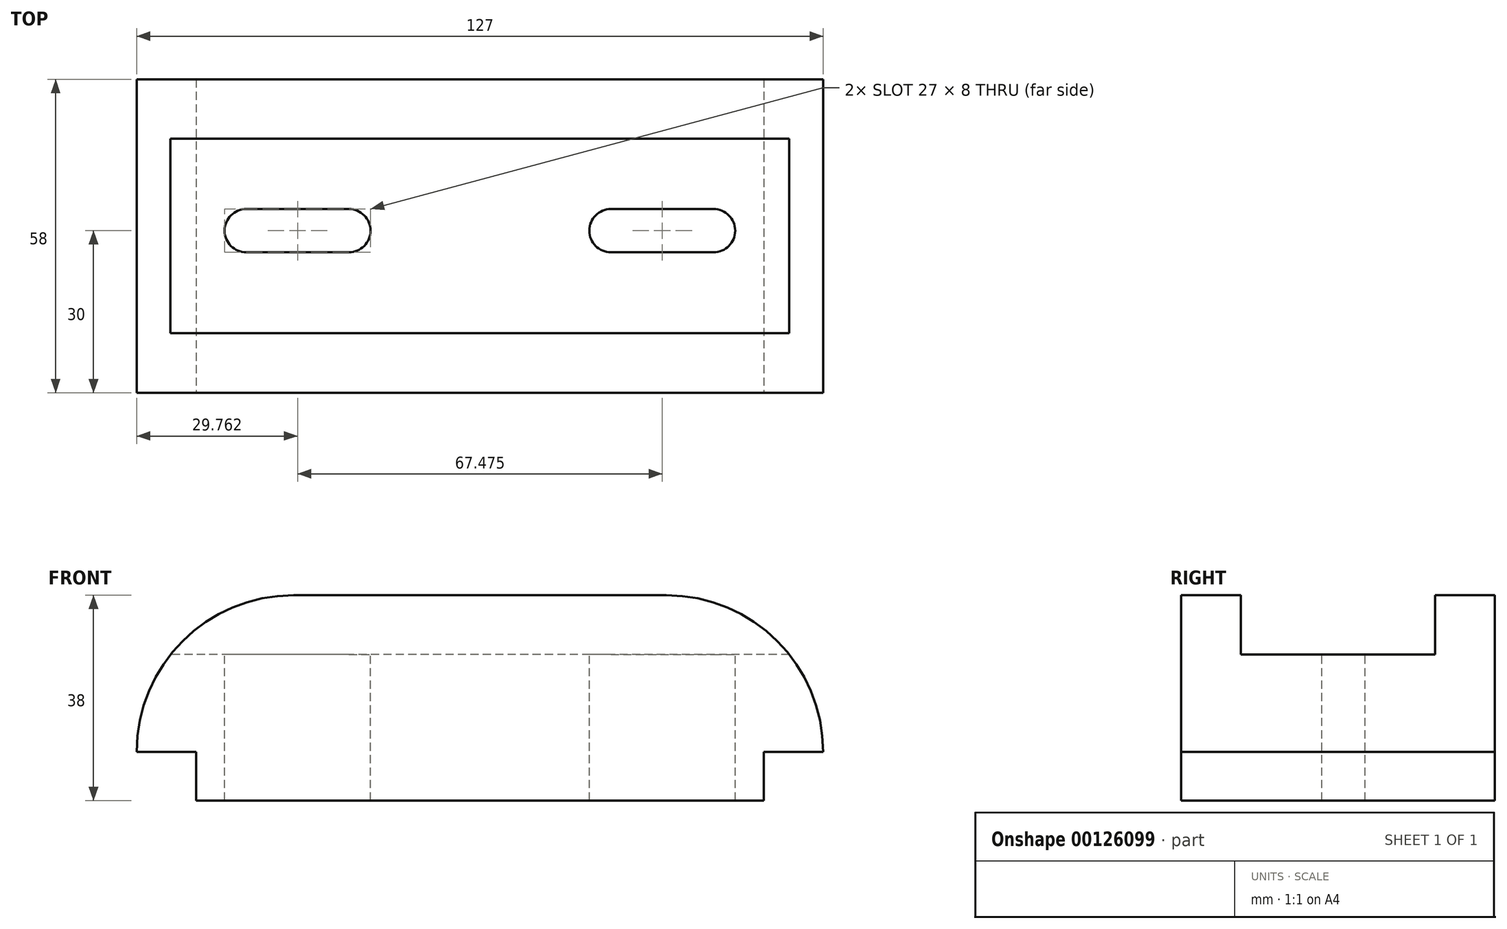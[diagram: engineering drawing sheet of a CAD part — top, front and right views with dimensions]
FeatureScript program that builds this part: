
annotation { "Feature Type Name" : "Feature", "Feature Type Description" : "" }
export const myFeature = defineFeature(function(context is Context, id is Id, definition is map)
    precondition{}
    {
        {
            var Q0;
            Q0=qCreatedBy(makeId("Front.planeOp"),FACE);
            var sketch = newSketch(context, id + "F0", { "sketchPlane" : qUnion([Q0])});
            skLineSegment(sketch, "E0", {"start": v(0, 72.55) * mm, "end": v(0, -38.1) * mm, "construction": true});
            skLineSegment(sketch, "E1", {"start": v(0, 38) * mm, "end": v(0, 0) * mm});
            skLineSegment(sketch, "E2", {"start": v(0, 0) * mm, "end": v(52.5, 0) * mm});
            skLineSegment(sketch, "E3", {"start": v(52.5, 0) * mm, "end": v(52.5, 9) * mm});
            skLineSegment(sketch, "E4", {"start": v(52.5, 9) * mm, "end": v(63.5, 9) * mm});
            skLineSegment(sketch, "E5", {"start": v(0, 38) * mm, "end": v(34.5, 38) * mm});
            skArc(sketch, "E6", {"start": v(34.5, 38) * mm, "mid": v(55, 29.5) * mm, "end": v(63.5, 9) * mm});
            skLineSegment(sketch, "E7.MirrorCS", {"start": v(0, 0) * mm, "end": v(-52.5, 0) * mm});
            skLineSegment(sketch, "E8.MirrorCS", {"start": v(-52.5, 0) * mm, "end": v(-52.5, 9) * mm});
            skLineSegment(sketch, "E9.MirrorCS", {"start": v(-52.5, 9) * mm, "end": v(-63.5, 9) * mm});
            skArc(sketch, "E10.MirrorCS", {"start": v(-34.5, 38) * mm, "mid": v(-55, 29.5) * mm, "end": v(-63.5, 9) * mm});
            skLineSegment(sketch, "E11.MirrorCS", {"start": v(0, 38) * mm, "end": v(-34.5, 38) * mm});
            skSolve(sketch);
        }
        {
            var Q0;
            Q0 = qSketchRegion(id + "F0", true);
            extrude(context, id + "F1", {"entities" : qUnion([Q0]), "oppositeDirection" : true, "depth" : 58 * mm});
        }
        {
            var Q0;
            Q0=makeQuery(id+"F1.opExtrude","SWEPT_FACE",FACE,{"disambiguationData":[OSD([sQuery(id+"F0.wireOp",EDGE,"E5"),sQuery(id+"F0.wireOp",EDGE,"E11.MirrorCS")])]});
            var sketch = newSketch(context, id + "F2", { "sketchPlane" : qUnion([Q0])});
            skLineSegment(sketch, "E12", {"start": v(0, 69.8) * mm, "end": v(0, -12.57) * mm, "construction": true});
            skPoint(sketch, "E12.startSnap0", {"position": v(0, 58) * mm});
            skPoint(sketch, "E12.endSnap0", {"position": v(0, 0) * mm});
            skLineSegment(sketch, "E13", {"start": v(63.5, 47) * mm, "end": v(63.5, 11) * mm});
            skLineSegment(sketch, "E14", {"start": v(63.5, 11) * mm, "end": v(0, 11) * mm});
            skLineSegment(sketch, "E15", {"start": v(0, 11) * mm, "end": v(0, 47) * mm});
            skLineSegment(sketch, "E16", {"start": v(0, 47) * mm, "end": v(63.5, 47) * mm});
            skLineSegment(sketch, "E17.MirrorCS", {"start": v(-63.5, 47) * mm, "end": v(-63.5, 11) * mm});
            skLineSegment(sketch, "E18.MirrorCS", {"start": v(-63.5, 11) * mm, "end": v(0, 11) * mm});
            skLineSegment(sketch, "E19.MirrorCS", {"start": v(0, 47) * mm, "end": v(-63.5, 47) * mm});
            skSolve(sketch);
        }
        {
            var Q0;
            Q0 = qSketchRegion(id + "F2", true);
            extrude(context, id + "F3", {"entities" : qUnion([Q0]), "operationType" : NewBodyOperationType.REMOVE, "oppositeDirection" : true, "depth" : 11 * mm});
        }
        {
            var Q0;
            Q0=makeQuery(id+"F3.boolean.opBoolean","COPY",FACE,{"derivedFrom":makeQuery(id+"F3.opExtrude","CAP_FACE",FACE,{"disambiguationData":[OSD([sQuery(id+"F2.wireOp",EDGE,"E13"),sQuery(id+"F2.wireOp",EDGE,"E14"),sQuery(id+"F2.wireOp",EDGE,"E16"),sQuery(id+"F2.wireOp",EDGE,"E17.MirrorCS"),sQuery(id+"F2.wireOp",EDGE,"E18.MirrorCS"),sQuery(id+"F2.wireOp",EDGE,"E19.MirrorCS")])],"isStart":false})});
            var sketch = newSketch(context, id + "F4", { "sketchPlane" : qUnion([Q0])});
            skLineSegment(sketch, "E20", {"start": v(24.24, 34) * mm, "end": v(43.24, 34) * mm});
            skLineSegment(sketch, "E21", {"start": v(24.24, 26) * mm, "end": v(43.24, 26) * mm});
            skArc(sketch, "E22", {"start": v(24.24, 34) * mm, "mid": v(20.24, 30) * mm, "end": v(24.24, 26) * mm});
            skArc(sketch, "E23", {"start": v(43.24, 34) * mm, "mid": v(47.24, 30) * mm, "end": v(43.24, 26) * mm});
            skLineSegment(sketch, "E24", {"start": v(0, 53.8) * mm, "end": v(0, -5.3) * mm, "construction": true});
            skPoint(sketch, "E24.endSnap0", {"position": v(0, 47) * mm});
            skArc(sketch, "E25.MirrorCS", {"start": v(-24.24, 34) * mm, "mid": v(-20.24, 30) * mm, "end": v(-24.24, 26) * mm});
            skArc(sketch, "E26.MirrorCS", {"start": v(-43.24, 34) * mm, "mid": v(-47.24, 30) * mm, "end": v(-43.24, 26) * mm});
            skLineSegment(sketch, "E27.MirrorCS", {"start": v(-24.24, 26) * mm, "end": v(-43.24, 26) * mm});
            skLineSegment(sketch, "E28.MirrorCS", {"start": v(-24.24, 34) * mm, "end": v(-43.24, 34) * mm});
            skSolve(sketch);
        }
        {
            var Q0;
            Q0 = qSketchRegion(id + "F4", true);
            extrude(context, id + "F5", {"entities" : qUnion([Q0]), "operationType" : NewBodyOperationType.REMOVE, "endBound" : BoundingType.THROUGH_ALL, "oppositeDirection" : true, "depth" : 25 * mm});
        }
    });
